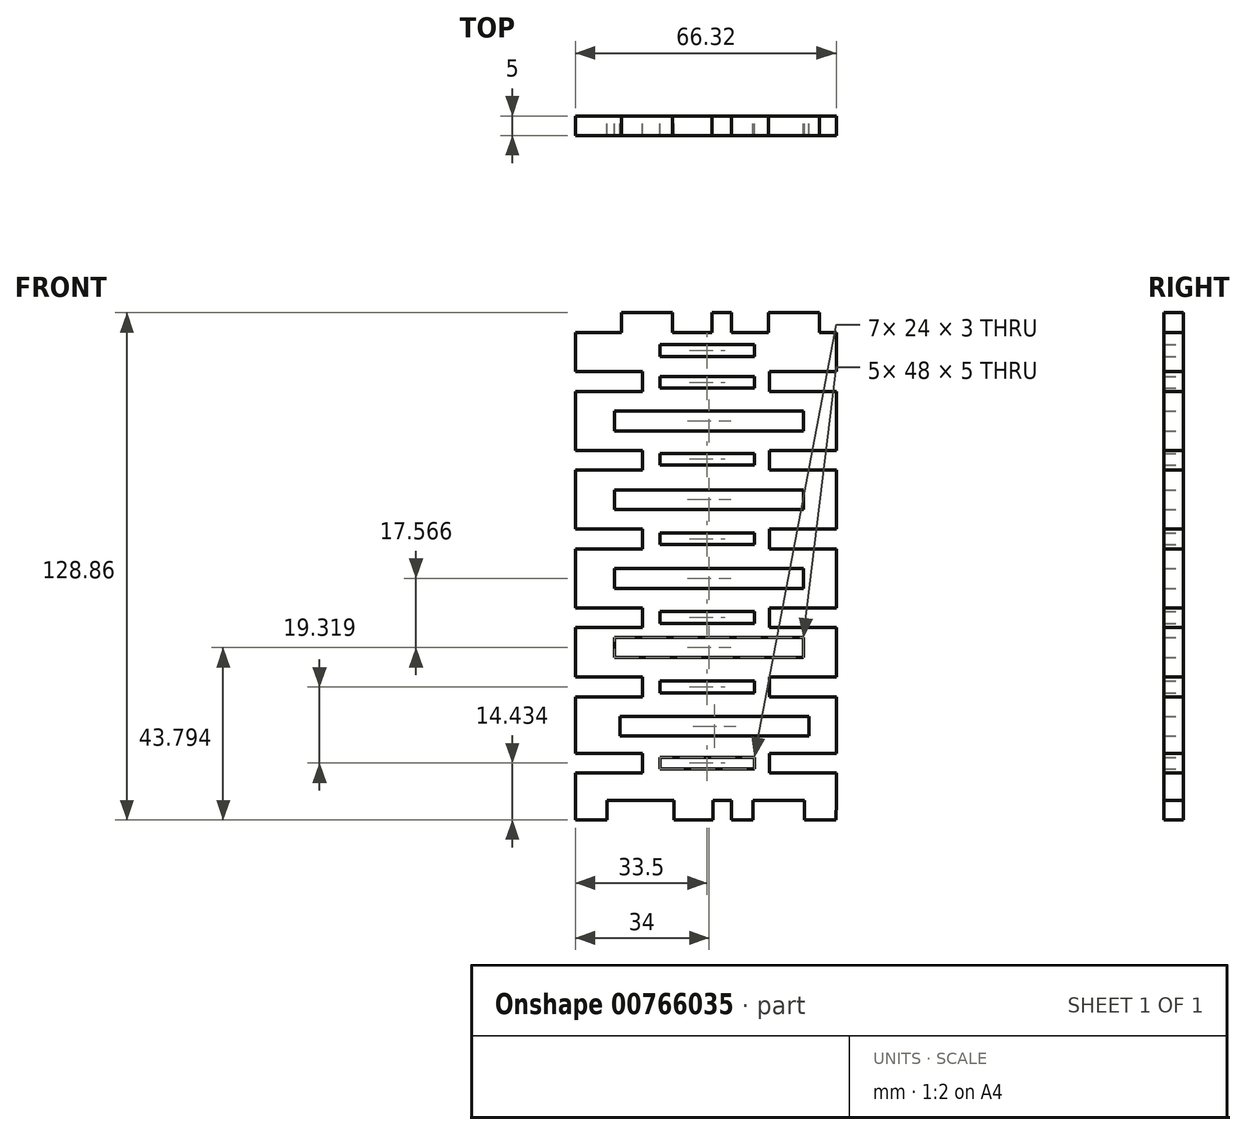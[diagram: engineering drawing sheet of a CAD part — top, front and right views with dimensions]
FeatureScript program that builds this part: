
annotation { "Feature Type Name" : "Feature", "Feature Type Description" : "" }
export const myFeature = defineFeature(function(context is Context, id is Id, definition is map)
    precondition{}
    {
        {
            var Q0;
            Q0=qCreatedBy(makeId("Front.planeOp"),FACE);
            var sketch = newSketch(context, id + "F0", { "sketchPlane" : qUnion([Q0])});
            skLineSegment(sketch, "E0.bottom", {"start": v(-55.86, 55) * mm, "end": v(10.46, 55) * mm});
            skLineSegment(sketch, "E0.top", {"start": v(-55.86, -63.86) * mm, "end": v(10.46, -63.86) * mm});
            skLineSegment(sketch, "E0.left", {"start": v(-55.86, 55) * mm, "end": v(-55.86, -63.86) * mm});
            skLineSegment(sketch, "E0.right", {"start": v(10.46, 55) * mm, "end": v(10.46, -63.86) * mm});
            skLineSegment(sketch, "E1", {"start": v(-55.86, 45) * mm, "end": v(-38.86, 45) * mm});
            skLineSegment(sketch, "E2", {"start": v(-38.86, 45) * mm, "end": v(-38.86, 40) * mm});
            skLineSegment(sketch, "E3", {"start": v(-38.86, 40) * mm, "end": v(-55.86, 40) * mm});
            skLineSegment(sketch, "E4", {"start": v(10.46, 45) * mm, "end": v(-6.54, 45) * mm});
            skLineSegment(sketch, "E5", {"start": v(-6.54, 45) * mm, "end": v(-6.54, 40) * mm});
            skLineSegment(sketch, "E6", {"start": v(-6.54, 40) * mm, "end": v(10.46, 40) * mm});
            skLineSegment(sketch, "E7", {"start": v(-45.86, 35) * mm, "end": v(2.14, 35) * mm});
            skLineSegment(sketch, "E8", {"start": v(2.14, 35) * mm, "end": v(2.14, 30) * mm});
            skLineSegment(sketch, "E9", {"start": v(2.14, 30) * mm, "end": v(-45.86, 30) * mm});
            skLineSegment(sketch, "E10", {"start": v(-45.86, 30) * mm, "end": v(-45.86, 35) * mm});
            skLineSegment(sketch, "E11", {"start": v(-55.86, 25) * mm, "end": v(-38.86, 25) * mm});
            skLineSegment(sketch, "E12", {"start": v(-38.86, 25) * mm, "end": v(-38.86, 20) * mm});
            skLineSegment(sketch, "E13", {"start": v(-38.86, 20) * mm, "end": v(-55.86, 20) * mm});
            skLineSegment(sketch, "E14", {"start": v(10.46, 25) * mm, "end": v(-6.54, 25) * mm});
            skLineSegment(sketch, "E15", {"start": v(-6.54, 25) * mm, "end": v(-6.54, 20) * mm});
            skLineSegment(sketch, "E16", {"start": v(-6.54, 20) * mm, "end": v(10.46, 20) * mm});
            skLineSegment(sketch, "E17", {"start": v(-44.15, 55) * mm, "end": v(-44.15, 60) * mm});
            skLineSegment(sketch, "E18", {"start": v(-44.15, 60) * mm, "end": v(-31.15, 60) * mm});
            skLineSegment(sketch, "E19", {"start": v(-31.15, 60) * mm, "end": v(-31.15, 55) * mm});
            skLineSegment(sketch, "E20", {"start": v(-6.83, 55) * mm, "end": v(-6.83, 60) * mm});
            skLineSegment(sketch, "E21", {"start": v(-6.83, 60) * mm, "end": v(6.17, 60) * mm});
            skLineSegment(sketch, "E22", {"start": v(6.17, 60) * mm, "end": v(6.17, 55) * mm});
            skLineSegment(sketch, "E23", {"start": v(-21.15, 55) * mm, "end": v(-21.15, 60) * mm});
            skLineSegment(sketch, "E24", {"start": v(-21.15, 60) * mm, "end": v(-16.15, 60) * mm});
            skLineSegment(sketch, "E25", {"start": v(-16.15, 60) * mm, "end": v(-16.15, 55) * mm});
            skLineSegment(sketch, "E26", {"start": v(-55.86, -63.86) * mm, "end": v(-55.86, -68.86) * mm});
            skLineSegment(sketch, "E27", {"start": v(-55.86, -68.86) * mm, "end": v(-47.86, -68.86) * mm});
            skLineSegment(sketch, "E28", {"start": v(-47.86, -68.86) * mm, "end": v(-47.86, -63.86) * mm});
            skLineSegment(sketch, "E29", {"start": v(2.31, -68.86) * mm, "end": v(2.31, -63.86) * mm});
            skLineSegment(sketch, "E30", {"start": v(2.31, -68.86) * mm, "end": v(10.31, -68.86) * mm});
            skLineSegment(sketch, "E31", {"start": v(10.31, -68.86) * mm, "end": v(10.46, -63.86) * mm});
            skLineSegment(sketch, "E32", {"start": v(-45.86, 15) * mm, "end": v(2.14, 15) * mm});
            skLineSegment(sketch, "E33", {"start": v(-45.86, 15) * mm, "end": v(-45.86, 10) * mm});
            skLineSegment(sketch, "E34", {"start": v(-45.86, 10) * mm, "end": v(2.14, 10) * mm});
            skLineSegment(sketch, "E35", {"start": v(2.14, 10) * mm, "end": v(2.14, 15) * mm});
            skLineSegment(sketch, "E36", {"start": v(-55.86, 5) * mm, "end": v(-38.86, 5) * mm});
            skLineSegment(sketch, "E37", {"start": v(-38.86, 5) * mm, "end": v(-38.86, 0) * mm});
            skLineSegment(sketch, "E38", {"start": v(-38.86, 0) * mm, "end": v(-55.86, 0) * mm});
            skLineSegment(sketch, "E39", {"start": v(10.46, 5) * mm, "end": v(-6.54, 5) * mm});
            skLineSegment(sketch, "E40", {"start": v(-6.54, 5) * mm, "end": v(-6.54, 0) * mm});
            skLineSegment(sketch, "E41", {"start": v(-6.54, 0) * mm, "end": v(10.46, 0) * mm});
            skLineSegment(sketch, "E42", {"start": v(-45.86, -5) * mm, "end": v(2.14, -5) * mm});
            skPoint(sketch, "E43.end.orphan", {"position": v(-20.84, -68.86) * mm});
            skPoint(sketch, "E43.start.orphan", {"position": v(-20.84, -63.86) * mm});
            skPoint(sketch, "E44.end.orphan", {"position": v(-30.84, -68.86) * mm});
            skPoint(sketch, "E44.start.orphan", {"position": v(-30.84, -63.86) * mm});
            skLineSegment(sketch, "E45", {"start": v(-30.84, -63.86) * mm, "end": v(-30.84, -68.86) * mm});
            skLineSegment(sketch, "E46", {"start": v(-20.84, -68.86) * mm, "end": v(-30.84, -68.86) * mm});
            skLineSegment(sketch, "E47", {"start": v(-20.84, -63.86) * mm, "end": v(-20.84, -68.86) * mm});
            skPoint(sketch, "E48.end.orphan", {"position": v(-16.15, -63.86) * mm});
            skPoint(sketch, "E49.start.orphan", {"position": v(-16.15, -68.86) * mm});
            skPoint(sketch, "E50.end.orphan", {"position": v(-10.69, -63.86) * mm});
            skPoint(sketch, "E50.start.orphan", {"position": v(-10.69, -68.86) * mm});
            skLineSegment(sketch, "E51", {"start": v(-16.15, -63.86) * mm, "end": v(-16.15, -68.86) * mm});
            skLineSegment(sketch, "E52", {"start": v(-10.69, -68.86) * mm, "end": v(-16.15, -68.86) * mm});
            skLineSegment(sketch, "E53", {"start": v(-10.69, -68.86) * mm, "end": v(-10.69, -63.86) * mm});
            skLineSegment(sketch, "E54", {"start": v(-45.86, -5) * mm, "end": v(-45.86, -10) * mm});
            skLineSegment(sketch, "E55", {"start": v(-45.86, -10) * mm, "end": v(2.14, -10) * mm});
            skLineSegment(sketch, "E56", {"start": v(2.14, -10) * mm, "end": v(2.14, -5) * mm});
            skLineSegment(sketch, "E57", {"start": v(-55.86, -15) * mm, "end": v(-38.86, -15) * mm});
            skLineSegment(sketch, "E58", {"start": v(-38.86, -15) * mm, "end": v(-38.86, -20) * mm});
            skLineSegment(sketch, "E59", {"start": v(-38.86, -20) * mm, "end": v(-55.86, -20) * mm});
            skLineSegment(sketch, "E60", {"start": v(10.46, -15) * mm, "end": v(-6.54, -15) * mm});
            skLineSegment(sketch, "E61", {"start": v(-6.54, -15) * mm, "end": v(-6.54, -20) * mm});
            skLineSegment(sketch, "E62", {"start": v(-6.54, -20) * mm, "end": v(10.46, -20) * mm});
            skLineSegment(sketch, "E63", {"start": v(-34.36, 51.88) * mm, "end": v(-34.36, 48.88) * mm});
            skLineSegment(sketch, "E64", {"start": v(-34.36, 48.88) * mm, "end": v(-10.36, 48.88) * mm});
            skLineSegment(sketch, "E65", {"start": v(-10.36, 48.88) * mm, "end": v(-10.36, 51.88) * mm});
            skLineSegment(sketch, "E66", {"start": v(-10.36, 51.88) * mm, "end": v(-34.36, 51.88) * mm});
            skLineSegment(sketch, "E67", {"start": v(-34.36, 43.82) * mm, "end": v(-34.36, 40.82) * mm});
            skLineSegment(sketch, "E68", {"start": v(-34.36, 40.82) * mm, "end": v(-10.36, 40.82) * mm});
            skLineSegment(sketch, "E69", {"start": v(-10.36, 40.82) * mm, "end": v(-10.36, 43.82) * mm});
            skLineSegment(sketch, "E70", {"start": v(-10.36, 43.82) * mm, "end": v(-34.36, 43.82) * mm});
            skLineSegment(sketch, "E71", {"start": v(-34.36, 24.27) * mm, "end": v(-34.36, 21.27) * mm});
            skLineSegment(sketch, "E72", {"start": v(-34.36, 21.27) * mm, "end": v(-10.36, 21.27) * mm});
            skLineSegment(sketch, "E73", {"start": v(-10.36, 21.27) * mm, "end": v(-10.36, 24.27) * mm});
            skLineSegment(sketch, "E74", {"start": v(-10.36, 24.27) * mm, "end": v(-34.36, 24.27) * mm});
            skLineSegment(sketch, "E75", {"start": v(-34.36, 4.07) * mm, "end": v(-34.36, 1.07) * mm});
            skLineSegment(sketch, "E76", {"start": v(-34.36, 1.07) * mm, "end": v(-10.36, 1.07) * mm});
            skLineSegment(sketch, "E77", {"start": v(-10.36, 1.07) * mm, "end": v(-10.36, 4.07) * mm});
            skLineSegment(sketch, "E78", {"start": v(-10.36, 4.07) * mm, "end": v(-34.36, 4.07) * mm});
            skLineSegment(sketch, "E79", {"start": v(-34.36, -15.92) * mm, "end": v(-34.36, -18.92) * mm});
            skLineSegment(sketch, "E80", {"start": v(-34.36, -18.92) * mm, "end": v(-10.36, -18.92) * mm});
            skLineSegment(sketch, "E81", {"start": v(-10.36, -18.92) * mm, "end": v(-10.36, -15.92) * mm});
            skLineSegment(sketch, "E82", {"start": v(-10.36, -15.92) * mm, "end": v(-34.36, -15.92) * mm});
            skLineSegment(sketch, "E83", {"start": v(-45.86, -22.57) * mm, "end": v(-45.86, -27.57) * mm});
            skLineSegment(sketch, "E84", {"start": v(-45.86, -27.57) * mm, "end": v(2.14, -27.57) * mm});
            skLineSegment(sketch, "E85", {"start": v(2.14, -27.57) * mm, "end": v(2.14, -22.57) * mm});
            skLineSegment(sketch, "E86", {"start": v(2.14, -22.57) * mm, "end": v(-45.86, -22.57) * mm});
            skLineSegment(sketch, "E87", {"start": v(-55.86, -32.57) * mm, "end": v(-38.86, -32.57) * mm});
            skLineSegment(sketch, "E88", {"start": v(-38.86, -32.57) * mm, "end": v(-38.86, -37.57) * mm});
            skLineSegment(sketch, "E89", {"start": v(-38.86, -37.57) * mm, "end": v(-55.86, -37.57) * mm});
            skLineSegment(sketch, "E90", {"start": v(10.46, -32.57) * mm, "end": v(-6.54, -32.57) * mm});
            skLineSegment(sketch, "E91", {"start": v(-6.54, -32.57) * mm, "end": v(-6.54, -37.57) * mm});
            skLineSegment(sketch, "E92", {"start": v(-6.54, -37.57) * mm, "end": v(10.46, -37.57) * mm});
            skLineSegment(sketch, "E93", {"start": v(-44.53, -42.57) * mm, "end": v(-44.53, -47.57) * mm});
            skLineSegment(sketch, "E94", {"start": v(-44.53, -47.57) * mm, "end": v(3.47, -47.57) * mm});
            skLineSegment(sketch, "E95", {"start": v(3.47, -47.57) * mm, "end": v(3.47, -42.57) * mm});
            skLineSegment(sketch, "E96", {"start": v(3.47, -42.57) * mm, "end": v(-44.53, -42.57) * mm});
            skLineSegment(sketch, "E97", {"start": v(-34.36, -33.6) * mm, "end": v(-34.36, -36.6) * mm});
            skLineSegment(sketch, "E98", {"start": v(-34.36, -36.6) * mm, "end": v(-10.36, -36.6) * mm});
            skLineSegment(sketch, "E99", {"start": v(-10.36, -36.6) * mm, "end": v(-10.36, -33.6) * mm});
            skLineSegment(sketch, "E100", {"start": v(-10.36, -33.6) * mm, "end": v(-34.36, -33.6) * mm});
            skLineSegment(sketch, "E101", {"start": v(-55.86, -51.92) * mm, "end": v(-38.86, -51.92) * mm});
            skLineSegment(sketch, "E102", {"start": v(-38.86, -51.92) * mm, "end": v(-38.86, -56.92) * mm});
            skLineSegment(sketch, "E103", {"start": v(-38.86, -56.92) * mm, "end": v(-55.86, -56.92) * mm});
            skLineSegment(sketch, "E104", {"start": v(10.46, -51.92) * mm, "end": v(-6.54, -51.92) * mm});
            skLineSegment(sketch, "E105", {"start": v(-6.54, -51.92) * mm, "end": v(-6.54, -56.92) * mm});
            skLineSegment(sketch, "E106", {"start": v(-6.54, -56.92) * mm, "end": v(10.46, -56.92) * mm});
            skLineSegment(sketch, "E107", {"start": v(-34.36, -52.93) * mm, "end": v(-34.36, -55.93) * mm});
            skLineSegment(sketch, "E108", {"start": v(-34.36, -55.93) * mm, "end": v(-10.36, -55.93) * mm});
            skLineSegment(sketch, "E109", {"start": v(-10.36, -55.93) * mm, "end": v(-10.36, -52.93) * mm});
            skLineSegment(sketch, "E110", {"start": v(-10.36, -52.93) * mm, "end": v(-34.36, -52.93) * mm});
            skLineSegment(sketch, "E111", {"start": v(10.46, 40) * mm, "end": v(10.46, 45) * mm});
            skLineSegment(sketch, "E112", {"start": v(10.46, 25) * mm, "end": v(10.46, 20) * mm});
            skLineSegment(sketch, "E113", {"start": v(10.46, 5) * mm, "end": v(10.46, 0) * mm});
            skLineSegment(sketch, "E114", {"start": v(10.46, -15) * mm, "end": v(10.46, -20) * mm});
            skLineSegment(sketch, "E115", {"start": v(-55.86, -15) * mm, "end": v(-55.86, -20) * mm});
            skLineSegment(sketch, "E116", {"start": v(-55.86, 5) * mm, "end": v(-55.86, 0) * mm});
            skLineSegment(sketch, "E117", {"start": v(-55.86, 25) * mm, "end": v(-55.86, 20) * mm});
            skLineSegment(sketch, "E118", {"start": v(-55.86, 45) * mm, "end": v(-55.86, 40) * mm});
            skLineSegment(sketch, "E119", {"start": v(-55.86, -51.92) * mm, "end": v(-55.86, -56.92) * mm});
            skLineSegment(sketch, "E120", {"start": v(10.46, -51.92) * mm, "end": v(10.46, -56.92) * mm});
            skLineSegment(sketch, "E121", {"start": v(10.46, -32.57) * mm, "end": v(10.46, -37.57) * mm});
            skLineSegment(sketch, "E122", {"start": v(-55.86, -32.57) * mm, "end": v(-55.86, -37.57) * mm});
            skSolve(sketch);
        }
        {
            var Q0;
            Q0=qCreatedBy(makeId("Front.planeOp"),FACE);
            var sketch = newSketch(context, id + "F1", { "sketchPlane" : qUnion([Q0])});
            skSolve(sketch);
        }
        {
            var Q0;
            Q0 = qSketchRegion(id + "F1", true);
            var Q1;
            {var subQ32=sQuery(id+"F0.wireOp",EDGE,"E1");Q1=makeQuery(id+"F0.imprint","IMPRINT",FACE,{"disambiguationData":[TD([[makeQuery(id+"F0.imprint","IMPRINT",EDGE,{"derivedFrom":subQ32}),1.0]])]});}
            var Q2;
            {var subQ0=sQuery(id+"F0.wireOp",EDGE,"E17");Q2=makeQuery(id+"F0.imprint","IMPRINT",FACE,{"disambiguationData":[TD([[makeQuery(id+"F0.imprint","IMPRINT",EDGE,{"derivedFrom":subQ0}),-1.0]])]});}
            var Q3;
            {var subQ0=sQuery(id+"F0.wireOp",EDGE,"E23");Q3=makeQuery(id+"F0.imprint","IMPRINT",FACE,{"disambiguationData":[TD([[makeQuery(id+"F0.imprint","IMPRINT",EDGE,{"derivedFrom":subQ0}),-1.0]])]});}
            var Q4;
            {var subQ0=sQuery(id+"F0.wireOp",EDGE,"E20");Q4=makeQuery(id+"F0.imprint","IMPRINT",FACE,{"disambiguationData":[TD([[makeQuery(id+"F0.imprint","IMPRINT",EDGE,{"derivedFrom":subQ0}),-1.0]])]});}
            var Q5;
            {var subQ0=sQuery(id+"F0.wireOp",EDGE,"E45");Q5=makeQuery(id+"F0.imprint","IMPRINT",FACE,{"disambiguationData":[TD([[makeQuery(id+"F0.imprint","IMPRINT",EDGE,{"derivedFrom":subQ0}),1.0]])]});}
            var Q6;
            {var subQ0=sQuery(id+"F0.wireOp",EDGE,"E51");Q6=makeQuery(id+"F0.imprint","IMPRINT",FACE,{"disambiguationData":[TD([[makeQuery(id+"F0.imprint","IMPRINT",EDGE,{"derivedFrom":subQ0}),1.0]])]});}
            var Q7;
            {var subQ2=sQuery(id+"F0.wireOp",EDGE,"E29");Q7=makeQuery(id+"F0.imprint","IMPRINT",FACE,{"disambiguationData":[TD([[makeQuery(id+"F0.imprint","IMPRINT",EDGE,{"derivedFrom":subQ2}),-1.0]])]});}
            var Q8;
            {var subQ0=sQuery(id+"F0.wireOp",EDGE,"E26");Q8=makeQuery(id+"F0.imprint","IMPRINT",FACE,{"disambiguationData":[TD([[makeQuery(id+"F0.imprint","IMPRINT",EDGE,{"derivedFrom":subQ0}),1.0]])]});}
            extrude(context, id + "F2", {"entities" : qUnion([Q0, Q1, Q2, Q3, Q4, Q5, Q6, Q7, Q8]), "depth" : 5 * mm, "offsetDistance" : 25 * mm});
        }
    });
